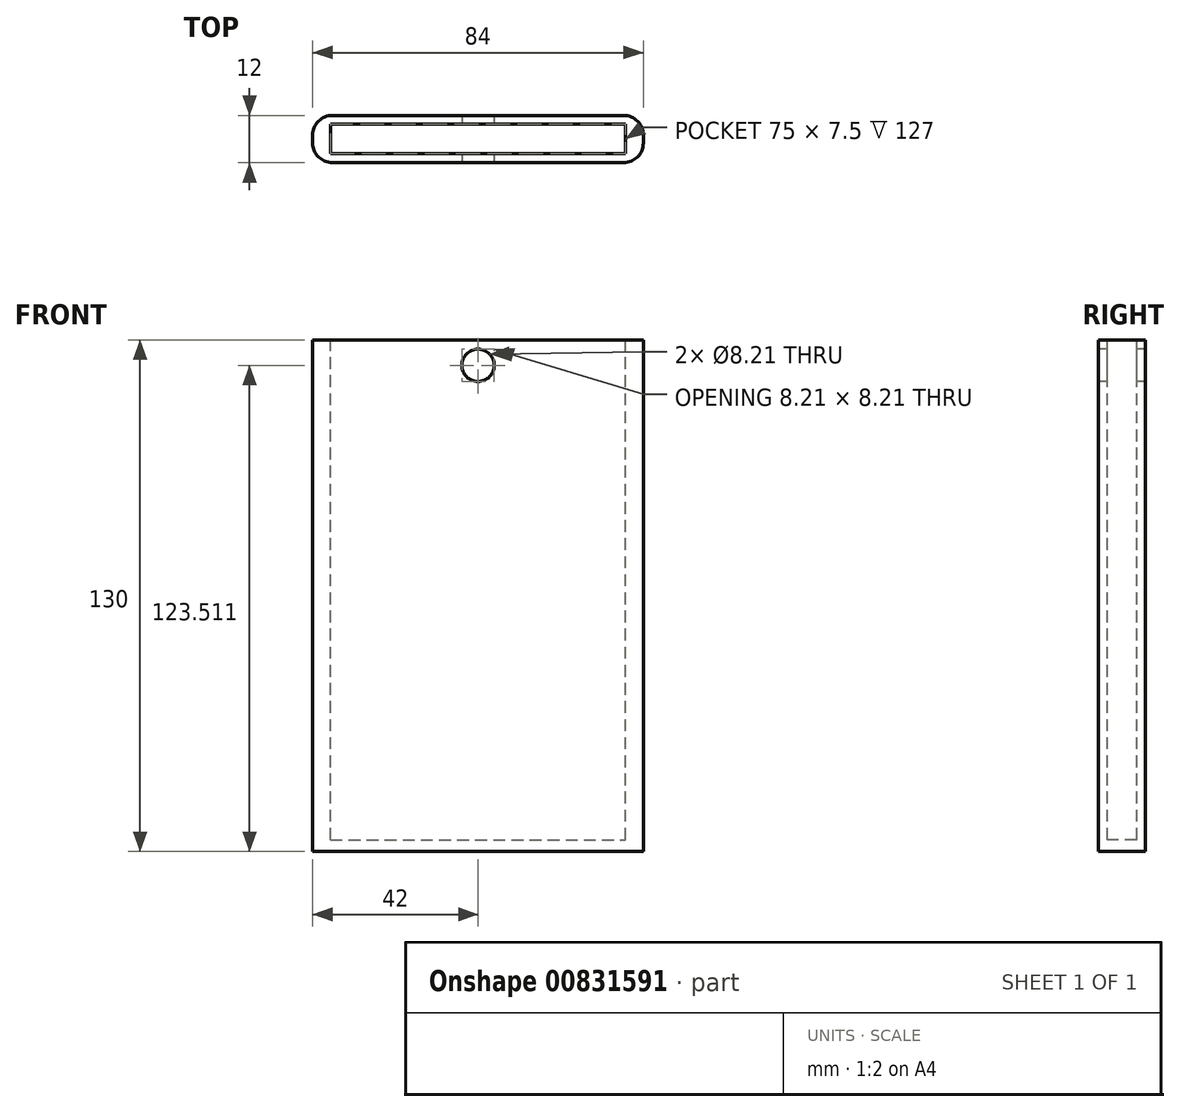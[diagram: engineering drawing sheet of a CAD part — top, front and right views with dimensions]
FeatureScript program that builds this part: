
annotation { "Feature Type Name" : "Feature", "Feature Type Description" : "" }
export const myFeature = defineFeature(function(context is Context, id is Id, definition is map)
    precondition{}
    {
        {
            var Q0;
            Q0=qCreatedBy(makeId("Top.planeOp"),FACE);
            var sketch = newSketch(context, id + "F0", { "sketchPlane" : qUnion([Q0])});
            skLineSegment(sketch, "E0.bottom", {"start": v(-42, 6) * mm, "end": v(42, 6) * mm});
            skLineSegment(sketch, "E0.top", {"start": v(-42, -6) * mm, "end": v(42, -6) * mm});
            skLineSegment(sketch, "E0.left", {"start": v(-42, 6) * mm, "end": v(-42, -6) * mm});
            skLineSegment(sketch, "E0.right", {"start": v(42, 6) * mm, "end": v(42, -6) * mm});
            skPoint(sketch, "E0.middle", {"position": v(0, 0) * mm});
            skSolve(sketch);
        }
        {
            var Q0;
            Q0=makeQuery(id+"F0.imprint","IMPRINT",FACE,{"disambiguationData":[TD([[makeQuery(id+"F0.imprint","IMPRINT",EDGE,{"derivedFrom":sQuery(id+"F0.wireOp",EDGE,"E0.bottom")}),-1.0]])]});
            extrude(context, id + "F1", {"entities" : qUnion([Q0]), "depth" : 130 * mm, "offsetDistance" : 25 * mm});
        }
        {
            var Q0;
            Q0=makeQuery(id+"F1.opExtrude","CAP_FACE",FACE,{"disambiguationData":[OSD([sQuery(id+"F0.wireOp",EDGE,"E0.bottom"),sQuery(id+"F0.wireOp",EDGE,"E0.top"),sQuery(id+"F0.wireOp",EDGE,"E0.left"),sQuery(id+"F0.wireOp",EDGE,"E0.right")])],"isStart":false});
            cPlane(context, id + "F2", {"entities" : qUnion([Q0]), "cplaneType" : CPlaneType.OFFSET, "offset" : 0 * mm, "width" : 150 * mm, "height" : 150 * mm});
        }
        {
            var Q0;
            Q0=qCreatedBy(id+"F2.planeOp",FACE);
            var sketch = newSketch(context, id + "F3", { "sketchPlane" : qUnion([Q0])});
            skLineSegment(sketch, "E1.bottom", {"start": v(-37.5, 3.75) * mm, "end": v(37.5, 3.75) * mm});
            skLineSegment(sketch, "E1.top", {"start": v(-37.5, -3.75) * mm, "end": v(37.5, -3.75) * mm});
            skLineSegment(sketch, "E1.left", {"start": v(-37.5, 3.75) * mm, "end": v(-37.5, -3.75) * mm});
            skLineSegment(sketch, "E1.right", {"start": v(37.5, 3.75) * mm, "end": v(37.5, -3.75) * mm});
            skPoint(sketch, "E1.middle", {"position": v(0, 0) * mm});
            skSolve(sketch);
        }
        {
            var Q0;
            Q0=makeQuery(id+"F3.imprint","IMPRINT",FACE,{"disambiguationData":[TD([[makeQuery(id+"F3.imprint","IMPRINT",EDGE,{"derivedFrom":sQuery(id+"F3.wireOp",EDGE,"E1.bottom")}),-1.0]])]});
            extrude(context, id + "F4", {"entities" : qUnion([Q0]), "operationType" : NewBodyOperationType.REMOVE, "oppositeDirection" : true, "depth" : 127 * mm, "offsetDistance" : 25 * mm});
        }
        {
            var Q0;
            Q0=makeQuery(id+"F1.opExtrude","SWEPT_EDGE",EDGE,{"disambiguationData":[OSD([sQuery(id+"F0.wireOp",EDGE,"E0.top"),sQuery(id+"F0.wireOp",EDGE,"E0.right")])]});
            var Q1;
            Q1=makeQuery(id+"F1.opExtrude","SWEPT_EDGE",EDGE,{"disambiguationData":[OSD([sQuery(id+"F0.wireOp",EDGE,"E0.bottom"),sQuery(id+"F0.wireOp",EDGE,"E0.right")])]});
            var Q2;
            Q2=makeQuery(id+"F1.opExtrude","SWEPT_EDGE",EDGE,{"disambiguationData":[OSD([sQuery(id+"F0.wireOp",EDGE,"E0.bottom"),sQuery(id+"F0.wireOp",EDGE,"E0.left")])]});
            var Q3;
            Q3=makeQuery(id+"F1.opExtrude","SWEPT_EDGE",EDGE,{"disambiguationData":[OSD([sQuery(id+"F0.wireOp",EDGE,"E0.top"),sQuery(id+"F0.wireOp",EDGE,"E0.left")])]});
            fillet(context, id + "F5", {"entities" : qUnion([Q0, Q1, Q2, Q3]), "radius" : 5 * mm, "tangentPropagation" : true, "allowEdgeOverflow" : false});
        }
        {
            var Q0;
            Q0=qCreatedBy(makeId("Front.planeOp"),FACE);
            var sketch = newSketch(context, id + "F6", { "sketchPlane" : qUnion([Q0])});
            skCircle(sketch, "E2", {"center": v(0, 123.51) * mm, "radius": 4.1 * mm});
            skSolve(sketch);
        }
        {
            var Q0;
            Q0 = qSketchRegion(id + "F6", true);
            extrude(context, id + "F7", {"entities" : qUnion([Q0]), "operationType" : NewBodyOperationType.REMOVE, "endBound" : BoundingType.THROUGH_ALL, "oppositeDirection" : true, "depth" : 25 * mm, "offsetDistance" : 25 * mm, "hasSecondDirection" : true, "secondDirectionOppositeDirection" : false, "secondDirectionDepth" : 25 * mm});
        }
    });
